# Revit family: LAMP_HANCE 48V 1000-2000 MEDIUM FLOOD DALI
name_source: partatom
category: Luminarias
revit_build: Autodesk Revit 2015 (Build: 20140606_1530(x64)
units: mm (PartAtom-declared; Revit-internal decimal feet)

## types (12) — shared parameters
CRI = 80
Comentarios de tipo = Availability of tilting between 0º and 90º, rotation between 0º and 355º and change ring color when placed in a project.
Diameter = 65 mm  [stored 0.213255 ft]
Elevación por defecto = 1219 mm
Fabricante = LAMP
Gear = Adjustable DALI
Height = 135 mm  [stored 0.442913 ft]
IEE = A+
Installation instructions = https://www.lamp.es
Insulation class = III
Lamp = COB LED
Last update = 02/04/2019
Luminaire type = Indoor - Spotlight
MacAdam = 3
Manufacturer URL = http://www.lamp.es
Manufacturer country = Spain
Manufacturer name = LAMP
Model explanation = Availability of tilting between 0º and 90º, rotation between 0º and 355º and change ring color when placed in a project.
Power Supply = 48V DC
Product URL = https://www.lamp.es
Product datasheet = http://www.lamp.es
Protection rating = IP20
Type = COB PHILIPS
Weight = 0.44 kg

## per-type parameters (varying)
| type | Descripción | Efficacy | Finish | Initial color | Initial intensity | LED Lifetime | Material tija | Modelo | Photometric web file | Plum | Power | Product code |
| 685LM 2700 MEDIUM FLOOD BLACK | HANCE TRACK 48 1000 VWW MFL DALI BK. | 73 lm/W | RAL9011 textured | 2700 K | 685 lm | 50.000 L90 B10 | LAMP_Aluminio Hance Negro | HS1TL10MF827DBB | Cuerpo Hance 48V BASE 1000_2000 (tilting)_MF : 685LM 2700 MEDIUM FLOOD BLACK | 9 W | 9 W | HS1TL10MF827DBB |
| 685LM 2700 MEDIUM FLOOD WHITE | HANCE TRACK 48 1000 VWW MFL DALI WH. | 73 lm/W | RAL9010 textured | 2700 K | 685 lm | 50.000 L90 B10 | LAMP_Aluminio Hance Blanco | HS1TL10MF827DBW | Cuerpo Hance 48V BASE 1000_2000 (tilting)_MF : 685LM 2700 MEDIUM FLOOD WHITE | 9 W | 9 W | HS1TL10MF827DBW |
| 699LM 3000 MEDIUM FLOOD BLACK | HANCE TRACK 48 1000 WW MFL DALI BK. | 74 lm/W | RAL9011 textured | 3000 K | 699 lm | 50.000 L90 B10 | LAMP_Aluminio Hance Negro | HS1TL10MF830DBB | Cuerpo Hance 48V BASE 1000_2000 (tilting)_MF : 699LM 3000 MEDIUM FLOOD BLACK | 9 W | 9 W | HS1TL10MF830DBB |
| 699LM 3000 MEDIUM FLOOD WHITE | HANCE TRACK 48 1000 WW MFL DALI WH. | 74 lm/W | RAL9010 textured | 3000 K | 699 lm | 50.000 L90 B10 | LAMP_Aluminio Hance Blanco | HS1TL10MF830DBW | Cuerpo Hance 48V BASE 1000_2000 (tilting)_MF : 699LM 3000 MEDIUM FLOOD WHITE | 9 W | 9 W | HS1TL10MF830DBW |
| 740LM 4000 MEDIUM FLOOD BLACK | HANCE TRACK 48 1000 NW MFL DALI BK. | 79 lm/W | RAL9011 textured | 4000 K | 740 lm | 50.000 L90 B10 | LAMP_Aluminio Hance Negro | HS1TL10MF840DBB | Cuerpo Hance 48V BASE 1000_2000 (tilting)_MF : 740LM 4000 MEDIUM FLOOD BLACK | 9 W | 9 W | HS1TL10MF840DBB |
| 740LM 4000 MEDIUM FLOOD WHITE | HANCE TRACK 48 1000 NW MFL DALI WH. | 79 lm/W | RAL9010 textured | 4000 K | 740 lm | 50.000 L90 B10 | LAMP_Aluminio Hance Blanco | HS1TL10MF840DBW | Cuerpo Hance 48V BASE 1000_2000 (tilting)_MF : 740LM 4000 MEDIUM FLOOD WHITE | 9 W | 9 W | HS1TL10MF840DBW |
| 1487LM 2700 MEDIUM FLOOD BLACK | HANCE TRACK 48 2000 VWW MFL DALI BK. | 88 lm/W | RAL9011 textured | 2700 K | 1487 lm | 50.000 L80 B10 | LAMP_Aluminio Hance Negro | HS1TL20MF827DBB | Cuerpo Hance 48V BASE 1000_2000 (tilting)_MF : 1487LM 2700 MEDIUM FLOOD BLACK | 17 W | 18 W | HS1TL20MF827DBB |
| 1487LM 2700 MEDIUM FLOOD WHITE | HANCE TRACK 48 2000 VWW MFL DALI WH. | 88 lm/W | RAL9010 textured | 2700 K | 1487 lm | 50.000 L80 B10 | LAMP_Aluminio Hance Blanco | HS1TL20MF827DBW | Cuerpo Hance 48V BASE 1000_2000 (tilting)_MF : 1487LM 2700 MEDIUM FLOOD WHITE | 17 W | 18 W | HS1TL20MF827DBW |
| 1517LM 3000 MEDIUM FLOOD BLACK | HANCE TRACK 48 2000 WW MFL DALI BK. | 90 lm/W | RAL9011 textured | 3000 K | 1517 lm | 50.000 L80 B10 | LAMP_Aluminio Hance Negro | HS1TL20MF830DBB | Cuerpo Hance 48V BASE 1000_2000 (tilting)_MF : 1517LM 3000 MEDIUM FLOOD BLACK | 17 W | 18 W | HS1TL20MF830DBB |
| 1517LM 3000 MEDIUM FLOOD WHITE | HANCE TRACK 48 2000 WW MFL DALI WH. | 90 lm/W | RAL9010 textured | 3000 K | 1517 lm | 50.000 L80 B10 | LAMP_Aluminio Hance Blanco | HS1TL20MF830DBW | Cuerpo Hance 48V BASE 1000_2000 (tilting)_MF : 1517LM 3000 MEDIUM FLOOD WHITE | 17 W | 18 W | HS1TL20MF830DBW |
| 1607LM 4000 MEDIUM FLOOD BLACK | HANCE TRACK 48 2000 NW MFL DALI BK. | 95 lm/W | RAL9011 textured | 4000 K | 1607 lm | 50.000 L80 B10 | LAMP_Aluminio Hance Negro | HS1TL20MF840DBB | Cuerpo Hance 48V BASE 1000_2000 (tilting)_MF : 1607LM 4000 MEDIUM FLOOD BLACK | 17 W | 18 W | HS1TL20MF840DBB |
| 1607LM 4000 MEDIUM FLOOD WHITE | HANCE TRACK 48 2000 NW MFL DALI WH. | 95 lm/W | RAL9010 textured | 4000 K | 1607 lm | 50.000 L80 B10 | LAMP_Aluminio Hance Blanco | HS1TL20MF840DBW | Cuerpo Hance 48V BASE 1000_2000 (tilting)_MF : 1607LM 4000 MEDIUM FLOOD WHITE | 17 W | 18 W | HS1TL20MF840DBW |

note: [stored X ft] marks values corroborated as IEEE doubles in the binary element streams (Revit-internal decimal feet)
